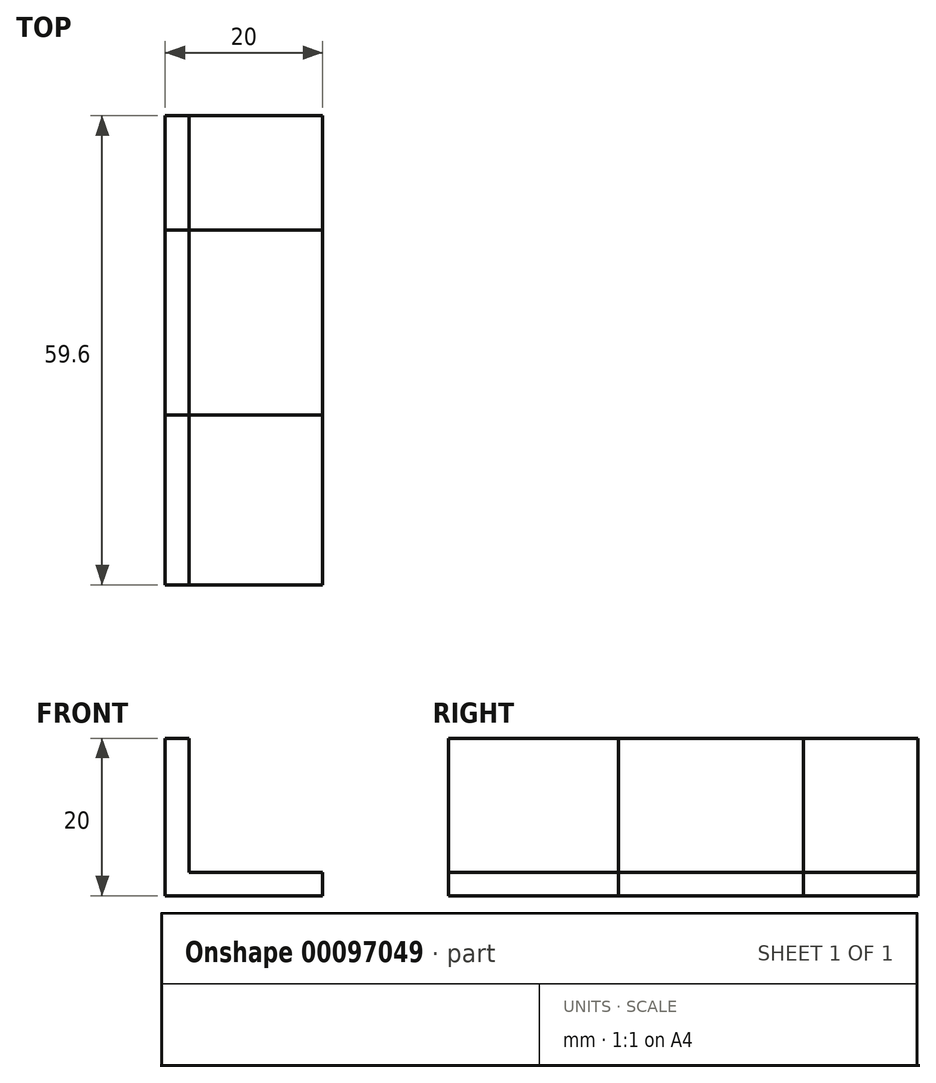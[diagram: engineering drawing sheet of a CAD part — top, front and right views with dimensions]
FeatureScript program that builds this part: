
annotation { "Feature Type Name" : "Feature", "Feature Type Description" : "" }
export const myFeature = defineFeature(function(context is Context, id is Id, definition is map)
    precondition{}
    {
        {
            var Q0;
            Q0=qCreatedBy(makeId("Front.planeOp"),FACE);
            var sketch = newSketch(context, id + "F0", { "sketchPlane" : qUnion([Q0])});
            skLineSegment(sketch, "E0", {"start": v(0, 0) * mm, "end": v(20, 0) * mm});
            skLineSegment(sketch, "E1", {"start": v(20, 0) * mm, "end": v(20, 3) * mm});
            skLineSegment(sketch, "E2", {"start": v(20, 3) * mm, "end": v(3, 3) * mm});
            skLineSegment(sketch, "E3", {"start": v(3, 3) * mm, "end": v(3, 20) * mm});
            skLineSegment(sketch, "E4", {"start": v(3, 20) * mm, "end": v(0, 20) * mm});
            skLineSegment(sketch, "E5", {"start": v(0, 20) * mm, "end": v(0, 0) * mm});
            skSolve(sketch);
        }
        {
            var Q0;
            Q0=qSketchRegion(id+"F0",true);
            extrude(context, id + "F1", {"entities" : qUnion([Q0]), "depth" : 14.5 * mm});
        }
        {
            var Q0;
            Q0=qSketchRegion(id+"F0",true);
            extrude(context, id + "F2", {"entities" : qUnion([Q0]), "depth" : 38 * mm});
        }
        {
            var Q0;
            Q0=qSketchRegion(id+"F0",true);
            extrude(context, id + "F3", {"entities" : qUnion([Q0]), "depth" : 59.6 * mm});
        }
    });
